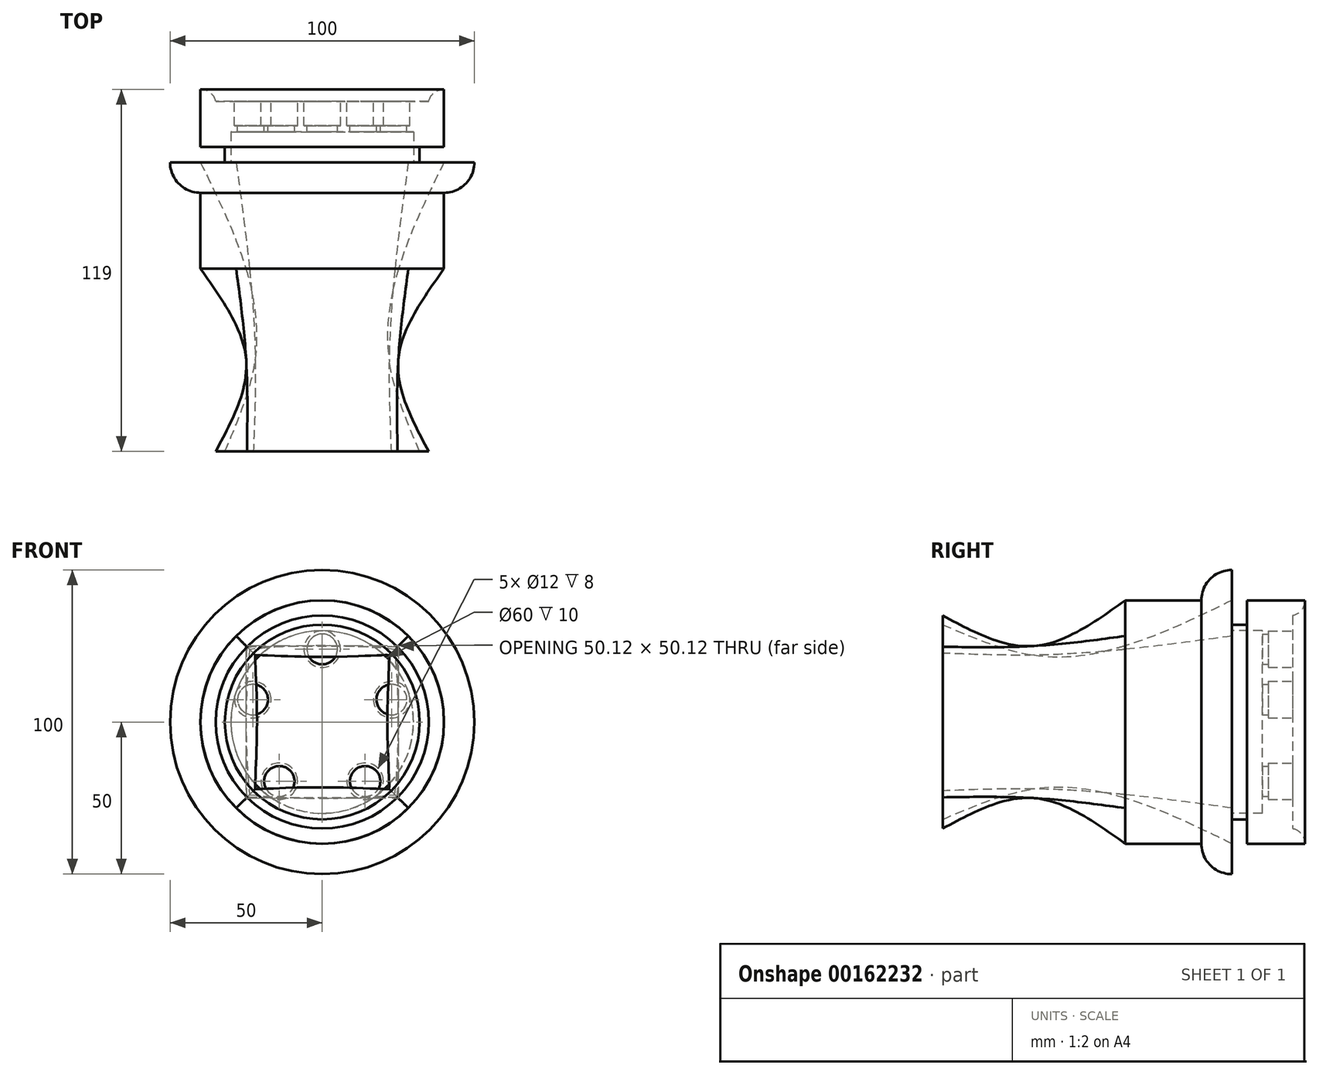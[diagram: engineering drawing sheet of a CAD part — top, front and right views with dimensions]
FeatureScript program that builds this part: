
annotation { "Feature Type Name" : "Feature", "Feature Type Description" : "" }
export const myFeature = defineFeature(function(context is Context, id is Id, definition is map)
    precondition{}
    {
        {
            var Q0;
            Q0=qCreatedBy(makeId("Front.planeOp"),FACE);
            var sketch = newSketch(context, id + "F0", { "sketchPlane" : qUnion([Q0])});
            skCircle(sketch, "E0", {"center": v(0, 0) * mm, "radius": 50 * mm});
            skSolve(sketch);
        }
        {
            var Q0;
            Q0 = qSketchRegion(id + "F0", true);
            extrude(context, id + "F1", {"entities" : qUnion([Q0]), "depth" : 10 * mm});
        }
        {
            var Q0;
            Q0=makeQuery(id+"F1.opExtrude","CAP_FACE",FACE,{"disambiguationData":[OSD([sQuery(id+"F0.wireOp",EDGE,"E0")])],"isStart":false});
            var sketch = newSketch(context, id + "F2", { "sketchPlane" : qUnion([Q0])});
            skCircle(sketch, "E1", {"center": v(0, 0) * mm, "radius": 40 * mm});
            skSolve(sketch);
        }
        {
            var Q0;
            Q0 = qSketchRegion(id + "F2", true);
            extrude(context, id + "F3", {"entities" : qUnion([Q0]), "operationType" : NewBodyOperationType.ADD, "depth" : 25 * mm});
        }
        {
            var Q0;
            Q0=makeQuery(id+"F1.opExtrude","CAP_EDGE",EDGE,{"disambiguationData":[OSD([sQuery(id+"F0.wireOp",EDGE,"E0")])],"isStart":false});
            fillet(context, id + "F4", {"entities" : qUnion([Q0]), "radius" : 10 * mm, "tangentPropagation" : true, "allowEdgeOverflow" : false});
        }
        {
            var Q0;
            Q0=makeQuery(id+"F3.opExtrude","CAP_FACE",FACE,{"disambiguationData":[OSD([sQuery(id+"F2.wireOp",EDGE,"E1")])],"isStart":false});
            cPlane(context, id + "F5", {"entities" : qUnion([Q0]), "cplaneType" : CPlaneType.OFFSET, "offset" : 30 * mm, "width" : 150 * mm, "height" : 150 * mm});
        }
        {
            var Q0;
            Q0=qCreatedBy(id+"F5.planeOp",FACE);
            cPlane(context, id + "F6", {"entities" : qUnion([Q0]), "cplaneType" : CPlaneType.OFFSET, "offset" : 30 * mm, "width" : 150 * mm, "height" : 150 * mm});
        }
        {
            var Q0;
            Q0=qCreatedBy(id+"F5.planeOp",FACE);
            var sketch = newSketch(context, id + "F7", { "sketchPlane" : qUnion([Q0])});
            skLineSegment(sketch, "E2.bottom", {"start": v(25, 25) * mm, "end": v(-25, 25) * mm});
            skLineSegment(sketch, "E2.top", {"start": v(25, -25) * mm, "end": v(-25, -25) * mm});
            skLineSegment(sketch, "E2.left", {"start": v(25, 25) * mm, "end": v(25, -25) * mm});
            skLineSegment(sketch, "E2.right", {"start": v(-25, 25) * mm, "end": v(-25, -25) * mm});
            skPoint(sketch, "E2.middle", {"position": v(0, 0) * mm});
            skSolve(sketch);
        }
        {
            var Q0;
            Q0=qCreatedBy(id+"F6.planeOp",FACE);
            var sketch = newSketch(context, id + "F8", { "sketchPlane" : qUnion([Q0])});
            skCircle(sketch, "E3", {"center": v(0, 0) * mm, "radius": 35 * mm});
            skSolve(sketch);
        }
        {
            var Q0;
            Q0=makeQuery(id+"F3.opExtrude","CAP_FACE",FACE,{"disambiguationData":[OSD([sQuery(id+"F2.wireOp",EDGE,"E1")])],"isStart":false});
            var Q1;
            Q1=makeQuery(id+"F7.imprint","IMPRINT",FACE,{"disambiguationData":[TD([[makeQuery(id+"F7.imprint","IMPRINT",EDGE,{"derivedFrom":sQuery(id+"F7.wireOp",EDGE,"E2.bottom")}),1.0]])]});
            var Q2;
            Q2=makeQuery(id+"F8.imprint","IMPRINT",FACE,{"disambiguationData":[TD([[makeQuery(id+"F8.imprint","IMPRINT",EDGE,{"derivedFrom":sQuery(id+"F8.wireOp",EDGE,"E3")}),1.0]])]});
            loft(context, id + "F9", {"sheetProfilesArray" : [{ "sheetProfileEntities" : qUnion([Q0]) }, { "sheetProfileEntities" : qUnion([Q1]) }, { "sheetProfileEntities" : qUnion([Q2]) }]});
        }
        {
            var Q0;
            Q0=qCreatedBy(id+"F5.planeOp",FACE);
            var sketch = newSketch(context, id + "F10", { "sketchPlane" : qUnion([Q0])});
            skLineSegment(sketch, "E4.bottom", {"start": v(22, 22) * mm, "end": v(-22, 22) * mm});
            skLineSegment(sketch, "E4.top", {"start": v(22, -22) * mm, "end": v(-22, -22) * mm});
            skLineSegment(sketch, "E4.left", {"start": v(22, 22) * mm, "end": v(22, -22) * mm});
            skLineSegment(sketch, "E4.right", {"start": v(-22, 22) * mm, "end": v(-22, -22) * mm});
            skPoint(sketch, "E4.middle", {"position": v(0, 0) * mm});
            skSolve(sketch);
        }
        {
            var Q0;
            Q0=makeQuery(id+"F9.opLoft","CAP_FACE",FACE,{"disambiguationData":[OSD([makeQuery(id+"F8.imprint","IMPRINT",FACE,{"disambiguationData":[TD([[makeQuery(id+"F8.imprint","IMPRINT",EDGE,{"derivedFrom":sQuery(id+"F8.wireOp",EDGE,"E3")}),1.0]])]})])],"isStart":true});
            var sketch = newSketch(context, id + "F11", { "sketchPlane" : qUnion([Q0])});
            skCircle(sketch, "E5", {"center": v(0, 0) * mm, "radius": 32 * mm});
            skSolve(sketch);
        }
        {
            var Q0;
            Q0=makeQuery(id+"F1.opExtrude","CAP_FACE",FACE,{"disambiguationData":[OSD([sQuery(id+"F0.wireOp",EDGE,"E0")])],"isStart":true});
            var sketch = newSketch(context, id + "F12", { "sketchPlane" : qUnion([Q0])});
            skCircle(sketch, "E6", {"center": v(0, 0) * mm, "radius": 40 * mm});
            skSolve(sketch);
        }
        {
            var Q1;
            Q1 = qSketchRegion(id + "F12", true);
            var Q2;
            Q2 = qSketchRegion(id + "F10", true);
            var Q3;
            Q3 = qSketchRegion(id + "F11", true);
            loft(context, id + "F13", {"operationType" : NewBodyOperationType.REMOVE, "sheetProfilesArray" : [{ "sheetProfileEntities" : qUnion([Q1]) }, { "sheetProfileEntities" : qUnion([Q2]) }, { "sheetProfileEntities" : qUnion([Q3]) }]});
        }
        {
            var Q0;
            Q0=qCreatedBy(makeId("Front.planeOp"),FACE);
            var sketch = newSketch(context, id + "F14", { "sketchPlane" : qUnion([Q0])});
            skCircle(sketch, "E7", {"center": v(0, 0) * mm, "radius": 32 * mm});
            skSolve(sketch);
        }
        {
            var Q0;
            Q0 = qSketchRegion(id + "F14", true);
            extrude(context, id + "F15", {"entities" : qUnion([Q0]), "oppositeDirection" : true, "depth" : 5 * mm});
        }
        {
            var Q0;
            Q0=makeQuery(id+"F15.opExtrude","CAP_FACE",FACE,{"disambiguationData":[OSD([sQuery(id+"F14.wireOp",EDGE,"E7")])],"isStart":false});
            var sketch = newSketch(context, id + "F16", { "sketchPlane" : qUnion([Q0])});
            skCircle(sketch, "E8", {"center": v(0, 0) * mm, "radius": 40 * mm});
            skSolve(sketch);
        }
        {
            var Q0;
            Q0 = qSketchRegion(id + "F16", true);
            extrude(context, id + "F17", {"entities" : qUnion([Q0]), "operationType" : NewBodyOperationType.ADD, "depth" : 15 * mm});
        }
        {
            var Q0;
            Q0=makeQuery(id+"F17.opExtrude","CAP_FACE",FACE,{"disambiguationData":[OSD([sQuery(id+"F16.wireOp",EDGE,"E8")])],"isStart":false});
            var sketch = newSketch(context, id + "F18", { "sketchPlane" : qUnion([Q0])});
            skCircle(sketch, "E9", {"center": v(0, 23.95) * mm, "radius": 4 * mm});
            skCircle(sketch, "E10.1.0", {"center": v(-22.83, 7.37) * mm, "radius": 4 * mm});
            skCircle(sketch, "E10.2.0", {"center": v(-14.1, -19.46) * mm, "radius": 4 * mm});
            skCircle(sketch, "E10.3.0", {"center": v(14.1, -19.46) * mm, "radius": 4 * mm});
            skCircle(sketch, "E10.4.0", {"center": v(22.83, 7.37) * mm, "radius": 4 * mm});
            skPoint(sketch, "E10.center", {"position": v(0, -0.05) * mm});
            skSolve(sketch);
        }
        {
            var Q0;
            Q0=sQuery(id+"F18.wireOp",VERTEX,"E9.center");
            var Q1;
            Q1=sQuery(id+"F18.wireOp",VERTEX,"E10.1.0.center");
            var Q2;
            Q2=sQuery(id+"F18.wireOp",VERTEX,"E10.2.0.center");
            var Q3;
            Q3=sQuery(id+"F18.wireOp",VERTEX,"E10.3.0.center");
            var Q4;
            Q4=sQuery(id+"F18.wireOp",VERTEX,"E10.4.0.center");
            var Q5;
            Q5=makeQuery(id+"F15.opExtrude","SWEPT_BODY",BODY,{"disambiguationData":[OSD([sQuery(id+"F14.wireOp",EDGE,"E7")])]});
            hole(context, id + "F19", {"style" : HoleStyle.C_BORE, "endStyle" : HoleEndStyle.BLIND, "holeDiameter" : 10 * mm, "cBoreDiameter" : 12 * mm, "cBoreDepth" : 8 * mm, "holeDepth" : 20 * mm, "startFromSketch" : true, "locations" : qUnion([Q0, Q1, Q2, Q3, Q4]), "scope" : qUnion([Q5])});
        }
        {
            var Q0;
            Q0=makeQuery(id+"F15.opExtrude","CAP_FACE",FACE,{"disambiguationData":[OSD([sQuery(id+"F14.wireOp",EDGE,"E7")])],"isStart":true});
            var sketch = newSketch(context, id + "F20", { "sketchPlane" : qUnion([Q0])});
            skCircle(sketch, "E11", {"center": v(0, 0) * mm, "radius": 30 * mm});
            skSolve(sketch);
        }
        {
            var Q0;
            Q0=makeQuery(id+"F20.imprint","IMPRINT",FACE,{"disambiguationData":[TD([[makeQuery(id+"F20.imprint","IMPRINT",EDGE,{"derivedFrom":sQuery(id+"F20.wireOp",EDGE,"E11")}),1.0]])]});
            extrude(context, id + "F21", {"entities" : qUnion([Q0]), "operationType" : NewBodyOperationType.REMOVE, "oppositeDirection" : true, "depth" : 10 * mm});
        }
        {
            var Q0;
            Q0=makeQuery(id+"F17.opExtrude","CAP_FACE",FACE,{"disambiguationData":[OSD([sQuery(id+"F16.wireOp",EDGE,"E8")])],"isStart":false});
            var sketch = newSketch(context, id + "F22", { "sketchPlane" : qUnion([Q0])});
            skCircle(sketch, "E12", {"center": v(0, 0) * mm, "radius": 40 * mm});
            skCircle(sketch, "E13", {"center": v(0, 0) * mm, "radius": 35 * mm});
            skSolve(sketch);
        }
        {
            var Q0;
            Q0=makeQuery(id+"F22.imprint","IMPRINT",FACE,{"disambiguationData":[TD([[makeQuery(id+"F22.imprint","IMPRINT",EDGE,{"derivedFrom":sQuery(id+"F22.wireOp",EDGE,"E12")}),1.0]])]});
            extrude(context, id + "F23", {"entities" : qUnion([Q0]), "operationType" : NewBodyOperationType.ADD, "depth" : 4 * mm});
        }
        {
            var Q0;
            Q0=makeQuery(id+"F23.opExtrude","CAP_EDGE",EDGE,{"disambiguationData":[OSD([sQuery(id+"F22.wireOp",EDGE,"E13")])],"isStart":false});
            fillet(context, id + "F24", {"entities" : qUnion([Q0]), "radius" : 5 * mm, "tangentPropagation" : true, "allowEdgeOverflow" : false});
        }
    });
